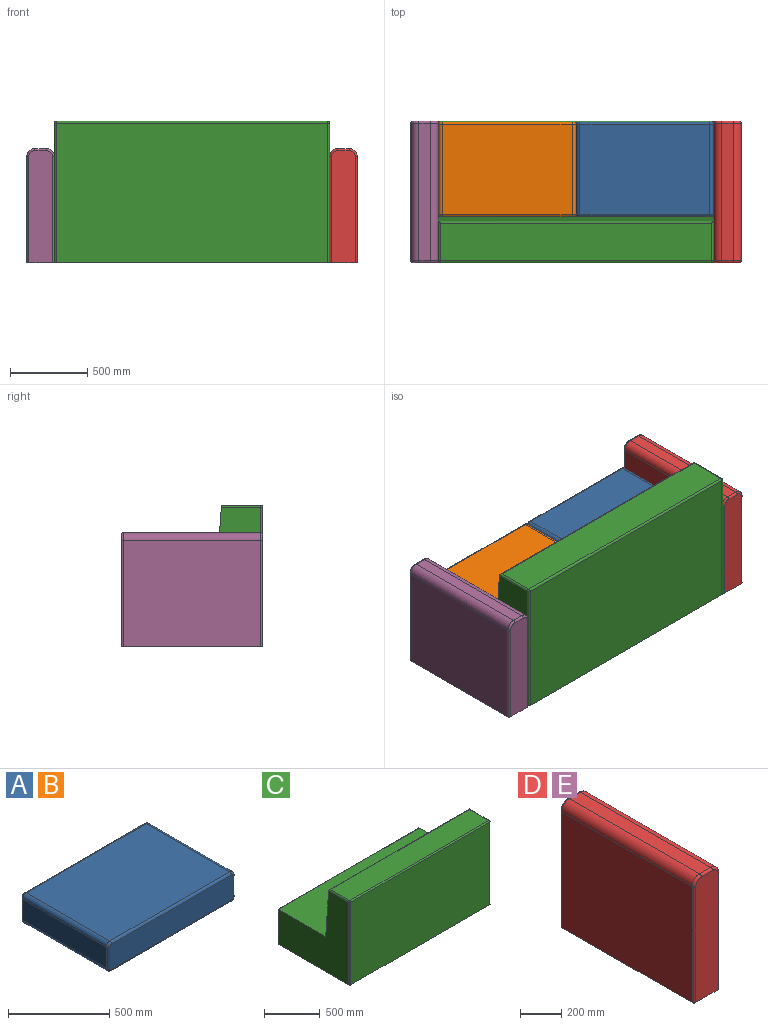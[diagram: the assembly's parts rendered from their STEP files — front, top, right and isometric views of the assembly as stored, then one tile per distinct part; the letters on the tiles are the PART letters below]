
ASSEMBLY  parts=5 mates=10
PART A: 26 faces, bbox 893.2x609.6x182 mm
  f0: plane 584.2x127mm, normal (-1,0,0), area 74193.4mm2, adj f1,f7,f11,f21
  f1: cylinder r=25.4mm len=584.2mm, axis (0,1,0), area 23308.5mm2, adj f0,f2,f13,f19
  f2: plane 838.2x584.2mm, normal (0,0,-1), area 489676.4mm2, adj f1,f3,f15,f18
  f3: cylinder r=25.4mm len=584.2mm, axis (0,1,0), area 23308.5mm2, adj f2,f4,f17,f20
  f4: plane 584.2x127mm, normal (1,0,0), area 74193.4mm2, adj f3,f5,f16,f22
  f5: cylinder r=25.4mm len=584.2mm, axis (0,1,0), area 23308.5mm2, adj f4,f6,f14,f24
  f6: plane 838.2x584.2mm, normal (0,0,1), area 489676.4mm2, adj f5,f7,f12,f25
  f7: cylinder r=25.4mm len=584.2mm, axis (0,1,0), area 23308.5mm2, adj f0,f6,f10,f23
  f8: plane 863.6x152.4mm, normal (0,-1,0), area 131474.2mm2, adj f18,f19,f20,f21,f22,f23,f24,f25
  f9: plane 863.6x152.4mm, normal (0,1,0), area 131474.2mm2, adj f10,f11,f12,f13,f14,f15,f16,f17
  f10: torus R=12.7mm, axis (0,-1,0), area 651.3mm2, adj f7,f9,f11,f12
  f11: cylinder r=12.7mm len=127mm, axis (0,0,-1), area 2533.5mm2, adj f0,f9,f10,f13
  f12: cylinder r=12.7mm len=838.2mm, axis (-1,0,0), area 16721.3mm2, adj f6,f9,f10,f14
  f13: torus R=12.7mm, axis (0,-1,0), area 651.3mm2, adj f1,f9,f11,f15
  f14: torus R=12.7mm, axis (0,-1,0), area 651.3mm2, adj f5,f9,f12,f16
  f15: cylinder r=12.7mm len=838.2mm, axis (1,0,0), area 16721.3mm2, adj f2,f9,f13,f17
  f16: cylinder r=12.7mm len=127mm, axis (0,0,1), area 2533.5mm2, adj f4,f9,f14,f17
  f17: torus R=12.7mm, axis (0,-1,0), area 651.3mm2, adj f3,f9,f15,f16
  f18: cylinder r=12.7mm len=838.2mm, axis (-1,0,0), area 16721.3mm2, adj f2,f8,f19,f20
  f19: torus R=12.7mm, axis (0,-1,0), area 651.3mm2, adj f1,f8,f18,f21
  f20: torus R=12.7mm, axis (0,-1,0), area 651.3mm2, adj f3,f8,f18,f22
  f21: cylinder r=12.7mm len=127mm, axis (0,0,1), area 2533.5mm2, adj f0,f8,f19,f23
  f22: cylinder r=12.7mm len=127mm, axis (0,0,-1), area 2533.5mm2, adj f4,f8,f20,f24
  f23: torus R=12.7mm, axis (0,-1,0), area 651.3mm2, adj f7,f8,f21,f25
  f24: torus R=12.7mm, axis (0,-1,0), area 651.3mm2, adj f5,f8,f22,f25
  f25: cylinder r=12.7mm len=838.2mm, axis (1,0,0), area 16721.3mm2, adj f6,f8,f23,f24
PART B: same geometry as A
PART C: 19 faces, bbox 1778x914.4x914.4 mm
  f0: plane 1752.6x242.17mm, normal (0,0,1), area 424435.5mm2, adj f8,f9,f12,f15
  f1: plane 1752.6x901.7mm, normal (0,-1,0), area 1580319.4mm2, adj f2,f10,f11,f15
  f2: plane 1778x914.4mm, normal (0,0,-1), area 1625664.7mm2, adj f1,f3,f6,f7,f10,f11,f16,f17
  f3: plane 1752.6x368.3mm, normal (0,1,0), area 645482.6mm2, adj f2,f16,f17,f18
  f4: plane 1778x596.9mm, normal (0,0,1), area 1061288.2mm2, adj f5,f6,f7,f18
  f5: plane 1778x521.61mm, normal (0,1,0.07), area 929776.2mm2, adj f4,f6,f7,f8,f9,f12
  f6: plane 901.7x889mm, normal (1,0,0), area 481122.3mm2, adj f2,f4,f5,f9,f10,f16
  f7: plane 901.7x889mm, normal (-1,0,0), area 481122.3mm2, adj f2,f4,f5,f11,f12,f17
  f8: cylinder r=12.7mm len=1777.94mm, axis (-1,0,0), area 33675.2mm2, adj f0,f5,f9,f12
  f9: cylinder r=12.7mm len=254.91mm, axis (0,1,0), area 4992.5mm2, adj f0,f5,f6,f8,f13
  f10: cylinder r=12.7mm len=901.7mm, axis (0,0,1), area 17988.1mm2, adj f1,f2,f6,f13
  f11: cylinder r=12.7mm len=901.7mm, axis (0,0,-1), area 17988.1mm2, adj f1,f2,f7,f14
  f12: cylinder r=12.7mm len=254.91mm, axis (0,-1,0), area 4992.5mm2, adj f0,f5,f7,f8,f14
  f13: sphere r=12.7mm, area 253.4mm2, adj f9,f10,f15
  f14: sphere r=12.7mm, area 253.4mm2, adj f11,f12,f15
  f15: cylinder r=12.7mm len=1752.6mm, axis (-1,0,0), area 34962.8mm2, adj f0,f1,f13,f14
  f16: cylinder r=12.7mm len=381mm, axis (0,0,-1), area 7508.5mm2, adj f2,f3,f6,f18
  f17: cylinder r=12.7mm len=381mm, axis (0,0,1), area 7508.5mm2, adj f2,f3,f7,f18
  f18: cylinder r=12.7mm len=1778mm, axis (-1,0,0), area 35285.4mm2, adj f3,f4,f16,f17
PART D: 18 faces, bbox 186.2x914.4x740.8 mm
  f0: plane 889x685.8mm, normal (-1,0,0), area 609676.2mm2, adj f1,f5,f12,f17
  f1: plane 914.4x177.8mm, normal (0,0,-1), area 162441.9mm2, adj f0,f2,f6,f7,f8,f12,f13,f17
  f2: plane 889x685.8mm, normal (1,0,0), area 609676.2mm2, adj f1,f3,f8,f13
  f3: cylinder r=50.8mm len=889mm, axis (0,1,0), area 70939mm2, adj f2,f4,f9,f14
  f4: plane 889x76.2mm, normal (0,0,1), area 67741.8mm2, adj f3,f5,f10,f15
  f5: cylinder r=50.8mm len=889mm, axis (0,1,0), area 70939mm2, adj f0,f4,f11,f16
  f6: plane 723.9x152.4mm, normal (0,-1,0), area 109699.3mm2, adj f1,f13,f14,f15,f16,f17
  f7: plane 723.9x152.4mm, normal (0,1,0), area 109699.3mm2, adj f1,f8,f9,f10,f11,f12
  f8: cylinder r=12.7mm len=685.8mm, axis (0,0,1), area 13681.1mm2, adj f1,f2,f7,f9
  f9: torus R=38.1mm, axis (0,-1,0), area 1447.3mm2, adj f3,f7,f8,f10
  f10: cylinder r=12.7mm len=76.2mm, axis (-1,0,0), area 1520.1mm2, adj f4,f7,f9,f11
  f11: torus R=38.1mm, axis (0,-1,0), area 1447.3mm2, adj f5,f7,f10,f12
  f12: cylinder r=12.7mm len=685.8mm, axis (0,0,-1), area 13681.1mm2, adj f0,f1,f7,f11
  f13: cylinder r=12.7mm len=685.8mm, axis (0,0,-1), area 13681.1mm2, adj f1,f2,f6,f14
  f14: torus R=38.1mm, axis (0,-1,0), area 1447.3mm2, adj f3,f6,f13,f15
  f15: cylinder r=12.7mm len=76.2mm, axis (1,0,0), area 1520.1mm2, adj f4,f6,f14,f16
  f16: torus R=38.1mm, axis (0,-1,0), area 1447.3mm2, adj f5,f6,f15,f17
  f17: cylinder r=12.7mm len=685.8mm, axis (0,0,1), area 13681.1mm2, adj f0,f1,f6,f16
PART E: same geometry as D
PLACE A t=(-32.53,-6.35,707.37)mm
PLACE B t=(-921.53,-6.35,707.37)mm
PLACE C t=(-1358.62,0,175.79)mm
PLACE D t=(1077.06,0,175.79)mm
PLACE E t=(-878.74,0,175.79)mm
MATE planar B.f0 <-> E.f2  axis (-1,0,0) through (-1358.62,-311.15,645.69)mm
MATE planar C.f6 <-> D.f0  axis (1,0,0) through (419.38,-901.7,175.79)mm
MATE planar D.f1 <-> C.f2  axis (0,0,-1) through (508.28,-457.2,175.79)mm
MATE planar E.f1 <-> C.f2  axis (0,0,-1) through (-1447.52,-457.2,175.79)mm
MATE planar A.f2 <-> C.f4  axis (0,0,-1) through (-25.12,-311.15,556.79)mm
MATE planar E.f2 <-> C.f7  axis (1,0,0) through (-1358.62,-457.2,518.69)mm
MATE planar A.f4 <-> D.f0  axis (1,0,0) through (419.38,-311.15,645.69)mm
MATE planar C.f3 <-> D.f7  axis (0,1,0) through (-469.62,0,359.94)mm
MATE planar B.f2 <-> C.f4  axis (0,0,-1) through (-914.12,-311.15,556.79)mm
MATE planar E.f6 <-> C.f1  axis (0,-1,0) through (-1523.72,-914.4,518.69)mm
